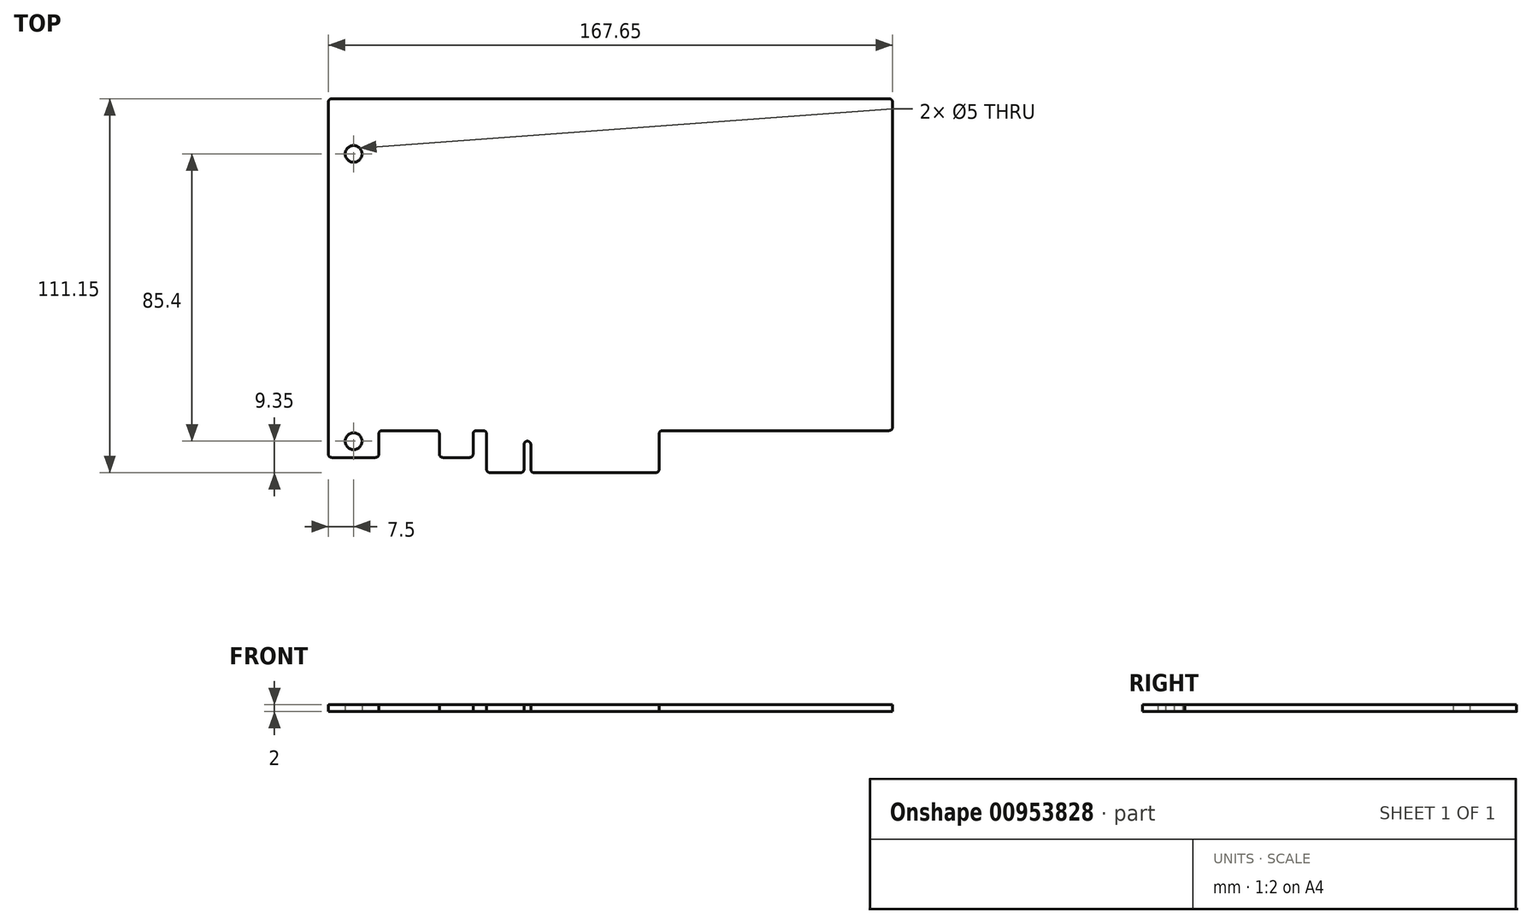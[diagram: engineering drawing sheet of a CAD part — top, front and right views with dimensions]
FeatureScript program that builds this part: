
annotation { "Feature Type Name" : "Feature", "Feature Type Description" : "" }
export const myFeature = defineFeature(function(context is Context, id is Id, definition is map)
    precondition{}
    {
        {
            var Q0;
            Q0=qCreatedBy(makeId("Top.planeOp"),FACE);
            var sketch = newSketch(context, id + "F0", { "sketchPlane" : qUnion([Q0])});
            skCircle(sketch, "E0", {"center": v(0, 0) * mm, "radius": 2.5 * mm});
            skCircle(sketch, "E1", {"center": v(0, 85.4) * mm, "radius": 2.5 * mm});
            skLineSegment(sketch, "E2", {"start": v(-7.5, -4.85) * mm, "end": v(-7.5, 101.8) * mm});
            skLineSegment(sketch, "E3", {"start": v(-7.5, 101.8) * mm, "end": v(160.15, 101.8) * mm});
            skLineSegment(sketch, "E4", {"start": v(160.15, 101.8) * mm, "end": v(160.15, 3.15) * mm});
            skLineSegment(sketch, "E5", {"start": v(160.15, 3.15) * mm, "end": v(90.8, 3.15) * mm});
            skLineSegment(sketch, "E6", {"start": v(90.8, 3.15) * mm, "end": v(90.8, -9.35) * mm});
            skLineSegment(sketch, "E7", {"start": v(50.65, -9.35) * mm, "end": v(50.65, 0) * mm});
            skLineSegment(sketch, "E8", {"start": v(52.65, 0) * mm, "end": v(50.65, 0) * mm});
            skLineSegment(sketch, "E9", {"start": v(52.65, 0) * mm, "end": v(52.65, -9.35) * mm});
            skLineSegment(sketch, "E10", {"start": v(39.5, -9.35) * mm, "end": v(39.5, 3.15) * mm});
            skLineSegment(sketch, "E11", {"start": v(39.5, 3.15) * mm, "end": v(35.5, 3.15) * mm});
            skLineSegment(sketch, "E12", {"start": v(35.5, 3.15) * mm, "end": v(35.5, -4.85) * mm});
            skLineSegment(sketch, "E13", {"start": v(35.5, -4.85) * mm, "end": v(25.5, -4.85) * mm});
            skLineSegment(sketch, "E14", {"start": v(25.5, -4.85) * mm, "end": v(25.5, 3.15) * mm});
            skLineSegment(sketch, "E15", {"start": v(25.5, 3.15) * mm, "end": v(7.5, 3.15) * mm});
            skLineSegment(sketch, "E16", {"start": v(7.5, 3.15) * mm, "end": v(7.5, -4.85) * mm});
            skLineSegment(sketch, "E17", {"start": v(7.5, -4.85) * mm, "end": v(-7.5, -4.85) * mm});
            skLineSegment(sketch, "E18", {"start": v(51.65, 0) * mm, "end": v(51.65, -9.35) * mm, "construction": true});
            skLineSegment(sketch, "E19", {"start": v(52.65, -9.35) * mm, "end": v(90.8, -9.35) * mm});
            skLineSegment(sketch, "E20", {"start": v(39.5, -9.35) * mm, "end": v(50.65, -9.35) * mm});
            skLineSegment(sketch, "E21", {"start": v(25.5, 3.15) * mm, "end": v(35.5, 3.15) * mm, "construction": true});
            skLineSegment(sketch, "E22", {"start": v(7.5, -4.85) * mm, "end": v(25.5, -4.85) * mm, "construction": true});
            skLineSegment(sketch, "E23", {"start": v(50.65, -9.35) * mm, "end": v(52.65, -9.35) * mm, "construction": true});
            skLineSegment(sketch, "E24", {"start": v(39.5, -9.35) * mm, "end": v(0, -9.35) * mm, "construction": true});
            skLineSegment(sketch, "E25", {"start": v(39.5, 3.15) * mm, "end": v(90.8, 3.15) * mm, "construction": true});
            skSolve(sketch);
        }
        {
            var Q0;
            Q0=qSketchRegion(id+"F0",true);
            extrude(context, id + "F1", {"entities" : qUnion([Q0]), "depth" : 2 * mm});
        }
        {
            var Q0;
            Q0=makeQuery(id+"F1.opExtrude","SWEPT_EDGE",EDGE,{"disambiguationData":[OSD([sQuery(id+"F0.wireOp",EDGE,"E2"),sQuery(id+"F0.wireOp",EDGE,"E17")])]});
            var Q1;
            Q1=makeQuery(id+"F1.opExtrude","SWEPT_EDGE",EDGE,{"disambiguationData":[OSD([sQuery(id+"F0.wireOp",EDGE,"E16"),sQuery(id+"F0.wireOp",EDGE,"E17")])]});
            var Q2;
            Q2=makeQuery(id+"F1.opExtrude","SWEPT_EDGE",EDGE,{"disambiguationData":[OSD([sQuery(id+"F0.wireOp",EDGE,"E14"),sQuery(id+"F0.wireOp",EDGE,"E15")])]});
            var Q3;
            Q3=makeQuery(id+"F1.opExtrude","SWEPT_EDGE",EDGE,{"disambiguationData":[OSD([sQuery(id+"F0.wireOp",EDGE,"E13"),sQuery(id+"F0.wireOp",EDGE,"E14")])]});
            var Q4;
            Q4=makeQuery(id+"F1.opExtrude","SWEPT_EDGE",EDGE,{"disambiguationData":[OSD([sQuery(id+"F0.wireOp",EDGE,"E12"),sQuery(id+"F0.wireOp",EDGE,"E13")])]});
            var Q5;
            Q5=makeQuery(id+"F1.opExtrude","SWEPT_EDGE",EDGE,{"disambiguationData":[OSD([sQuery(id+"F0.wireOp",EDGE,"E10"),sQuery(id+"F0.wireOp",EDGE,"E11")])]});
            var Q6;
            Q6=makeQuery(id+"F1.opExtrude","SWEPT_EDGE",EDGE,{"disambiguationData":[OSD([sQuery(id+"F0.wireOp",EDGE,"E10"),sQuery(id+"F0.wireOp",EDGE,"E20")])]});
            var Q7;
            Q7=makeQuery(id+"F1.opExtrude","SWEPT_EDGE",EDGE,{"disambiguationData":[OSD([sQuery(id+"F0.wireOp",EDGE,"E7"),sQuery(id+"F0.wireOp",EDGE,"E20")])]});
            var Q8;
            Q8=makeQuery(id+"F1.opExtrude","SWEPT_EDGE",EDGE,{"disambiguationData":[OSD([sQuery(id+"F0.wireOp",EDGE,"E8"),sQuery(id+"F0.wireOp",EDGE,"E9")])]});
            var Q9;
            Q9=makeQuery(id+"F1.opExtrude","SWEPT_EDGE",EDGE,{"disambiguationData":[OSD([sQuery(id+"F0.wireOp",EDGE,"E9"),sQuery(id+"F0.wireOp",EDGE,"E19")])]});
            var Q10;
            Q10=makeQuery(id+"F1.opExtrude","SWEPT_EDGE",EDGE,{"disambiguationData":[OSD([sQuery(id+"F0.wireOp",EDGE,"E6"),sQuery(id+"F0.wireOp",EDGE,"E19")])]});
            var Q11;
            Q11=makeQuery(id+"F1.opExtrude","SWEPT_EDGE",EDGE,{"disambiguationData":[OSD([sQuery(id+"F0.wireOp",EDGE,"E2"),sQuery(id+"F0.wireOp",EDGE,"E3")])]});
            var Q12;
            Q12=makeQuery(id+"F1.opExtrude","SWEPT_EDGE",EDGE,{"disambiguationData":[OSD([sQuery(id+"F0.wireOp",EDGE,"E3"),sQuery(id+"F0.wireOp",EDGE,"E4")])]});
            var Q13;
            Q13=makeQuery(id+"F1.opExtrude","SWEPT_EDGE",EDGE,{"disambiguationData":[OSD([sQuery(id+"F0.wireOp",EDGE,"E4"),sQuery(id+"F0.wireOp",EDGE,"E5")])]});
            var Q14;
            Q14=makeQuery(id+"F1.opExtrude","SWEPT_EDGE",EDGE,{"disambiguationData":[OSD([sQuery(id+"F0.wireOp",EDGE,"E5"),sQuery(id+"F0.wireOp",EDGE,"E6")])]});
            var Q15;
            Q15=makeQuery(id+"F1.opExtrude","SWEPT_EDGE",EDGE,{"disambiguationData":[OSD([sQuery(id+"F0.wireOp",EDGE,"E11"),sQuery(id+"F0.wireOp",EDGE,"E12")])]});
            var Q16;
            Q16=makeQuery(id+"F1.opExtrude","SWEPT_EDGE",EDGE,{"disambiguationData":[OSD([sQuery(id+"F0.wireOp",EDGE,"E15"),sQuery(id+"F0.wireOp",EDGE,"E16")])]});
            var Q17;
            Q17=makeQuery(id+"F1.opExtrude","SWEPT_EDGE",EDGE,{"disambiguationData":[OSD([sQuery(id+"F0.wireOp",EDGE,"E7"),sQuery(id+"F0.wireOp",EDGE,"E8")])]});
            fillet(context, id + "F2", {"entities" : qUnion([Q0, Q1, Q2, Q3, Q4, Q5, Q6, Q7, Q8, Q9, Q10, Q11, Q12, Q13, Q14, Q15, Q16, Q17]), "radius" : 1 * mm, "tangentPropagation" : true, "allowEdgeOverflow" : false});
        }
    });
